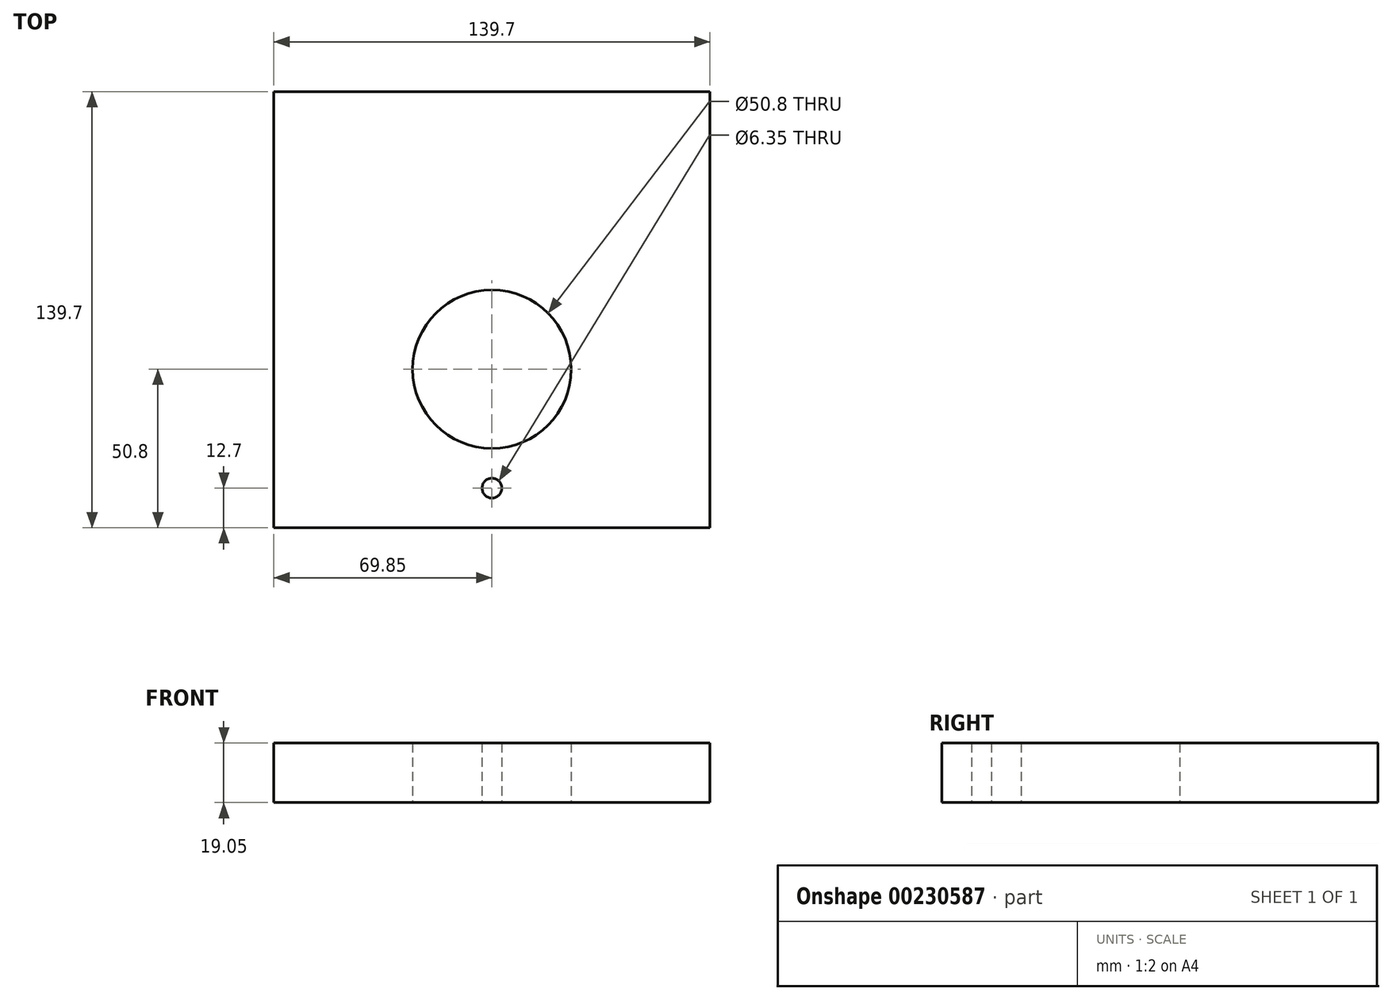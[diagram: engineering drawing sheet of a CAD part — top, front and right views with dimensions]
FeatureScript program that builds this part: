
annotation { "Feature Type Name" : "Feature", "Feature Type Description" : "" }
export const myFeature = defineFeature(function(context is Context, id is Id, definition is map)
    precondition{}
    {
        {
            var Q0;
            Q0=qCreatedBy(makeId("Top.planeOp"),FACE);
            var sketch = newSketch(context, id + "F0", { "sketchPlane" : qUnion([Q0])});
            skLineSegment(sketch, "E0.bottom", {"start": v(-69.85, 69.85) * mm, "end": v(69.85, 69.85) * mm});
            skLineSegment(sketch, "E0.top", {"start": v(-69.85, -69.85) * mm, "end": v(69.85, -69.85) * mm});
            skLineSegment(sketch, "E0.left", {"start": v(-69.85, 69.85) * mm, "end": v(-69.85, -69.85) * mm});
            skLineSegment(sketch, "E0.right", {"start": v(69.85, 69.85) * mm, "end": v(69.85, -69.85) * mm});
            skPoint(sketch, "E0.middle", {"position": v(0, 0) * mm});
            skCircle(sketch, "E1", {"center": v(0, -19.05) * mm, "radius": 25.4 * mm});
            skCircle(sketch, "E2", {"center": v(0, -57.15) * mm, "radius": 3.18 * mm});
            skSolve(sketch);
        }
        {
            var Q0;
            Q0 = qSketchRegion(id + "F0", true);
            extrude(context, id + "F1", {"entities" : qUnion([Q0]), "depth" : 19.05 * mm});
        }
    });
